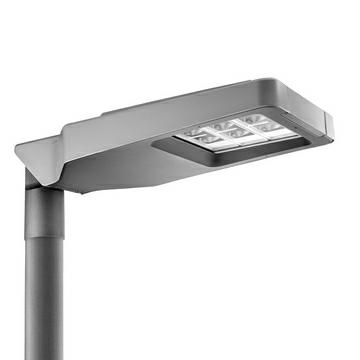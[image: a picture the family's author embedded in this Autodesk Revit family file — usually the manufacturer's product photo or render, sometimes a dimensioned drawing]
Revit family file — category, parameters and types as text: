
# Revit family: Lighting-Stradale-GEWISS-ROAD[5]MEDIUM-LED_OTTICA_HUGE_CLII
name_source: partatom
category: Apparecchi per illuminazione
units: mm (PartAtom-declared; Revit-internal decimal feet)

## family parameters
Basato su piano di lavoro = No
Condiviso = No
Punto di calcolo locali = No
Quota connettore circolare = Usa diametro
Sempre verticale = Sì
Sorgente d'illuminazione = No
Taglio con vuoti quando caricato = No
Tipo di parte = Normale

## types (1)
- Lighting-Stradale-GEWISS-ROAD[5]MEDIUM-LED_OTTICA_HUGE_CLII
    Alimentatore = Incluso
    Apparecchio a ridotta temperatura superficiale = -
    Applicazione = Esterno
    Cablaggio = Sezionatore
    Caratteristiche elettriche e gestione della luce = -
    Caratteristiche ottiche e illuminotecniche = -
    Catalogo = LIGHTING
    Catalogo Serie = ROAD [5]
    Certificazione DIN 18032-3 = -
    Certificazioni e classificazioni = -
    Classe fotobiologica = RG0
    Classe isolamento = II
    Classificazione: = -
    Codice Electrocod = 244C
    Codice digitale univoco (Datamatrix) = Attualmente non presente
    Colore = Grigio grafite
    Contesto = Illuminazione stradale e parcheggi
    Controllo abbagliamento e luminanza = G*3 - ULOR = 0
    Corpo = Alluminio pressofuso
    Corrente di pilotaggio. = 0,7A
    Descrizione = GWR5176V - ROAD5 MEDI HUGE V 6M 4000K 0,7A CL2
    Dispositivo di protezione = DM 10KV / CM 10KV
    Distanza minima dall'oggetto illuminato = 1M
    Durata di vita = L90B10 (Tq+25°C) = 100.000 h - L90B10 (Tq+50°C) = 50.000 h
    Efficienza luminosa (lm/W) = 111
    Finitura colore = Verniciato a polveri
    Fissaggio = Testa palo - Sbraccio
    Flusso nominale (lm) = 18720
    Frequenza nominale (Hz) = 50 / 60
    Gancio di chiusura = Maniglia frontale integrata
    Garanzia = 5 anni
    Grado di protezione = IP66
    Gruppo ottico = Riflettore in PC metallizzato
    Guarnizioni = silicone antinvecchiamento
    IDF = be49c13a-226b-4871-be31-40b900ed65a7
    IDT = ab01e1b5e8824c1da94a21a5ceb91f42
    IPEA = STRADALE = A+ // GRANDI AREE = A4+ // CICLOPEDONALI = A+ // AREE VERDI = A+ // CENTRO STORICO = A6+
    Immagine tipo = GWR5276M.jpg
    Inclinazione = -20° ÷ +10° sbraccio - -10° ÷ +20° testa palo
    Indice di resa cromatica = CRI-70
    Informazioni generali = -
    Installazione e manutenzione = -
    LED Life Time (L80B05) = 120000H
    Lampada = LED
    Lampada: = LED
    Lumen output (lm) = 17900
    Materiali = -
    Modello = GWR5176V
    Norma di riferimento = EN 60598-2-3, EN 60598-1 IEC/TR 62778
    Numero moduli = 6 (6x3 LED)
    Ottica = HUGE
    Peso (kg): = 9,09999999999999
    Potenza assorbita : = 161 W @ 0.7A
    Potenza di sistema = 159W
    Produttore = GEWISS S.p.A.
    Regolazione inclinazione = -20° ÷ +10° sbraccio - -10° ÷ +20° testa palo
    Resistenza agli urti = IK08
    Resistenza al filo incandescente = -
    SEO = Stradale
    Scheda Tecnica = https://www.gewiss.com
    Schermo = Vetro piano temperato spessore 4mm
    Sistema di controllo = DALI - 5 Step
    Sostituibilità gruppo ottico = Non disponibile
    Sostituibilità piastra di cablaggio = Non disponibile
    Superficie massima esposta al vento = 0,19M2
    Superficie massima esposta al vento : = 0.19 m2
    Temperatura di colore = 4000K
    Temperatura di colore: = 4000 K (CRI>70)
    Temperatura di esercizio = -25 +50 °C
    Temperatura di stoccaggio = -
    Temperatura di utilizzo = -25 +40 °C
    Tensione = 220/240 V - 50/60 Hz - Stand alone e/o Programmabile
    Tensione di alimentazione = 220 - 240 V
    Tipo di apparecchio = Apparecchiatura stradale a LED
    Tipo di installazione e montaggio = Testa palo - Sbraccio
    Tipologia = Programmabile (5 passi)
    Tipologia sorgente luminosa = LED - Non sostituibile
    Tolleranza cromatica = SDCM = 5
    URL = https://www.gewiss.com
    Vano di alimentazione = Integrato
    Versione file RFA = 20.11
    Viti esterne = Acciaio inox

## geometry (parser evidence)
native form markers: Blend x2
no freeform markers — native parametric forms only
